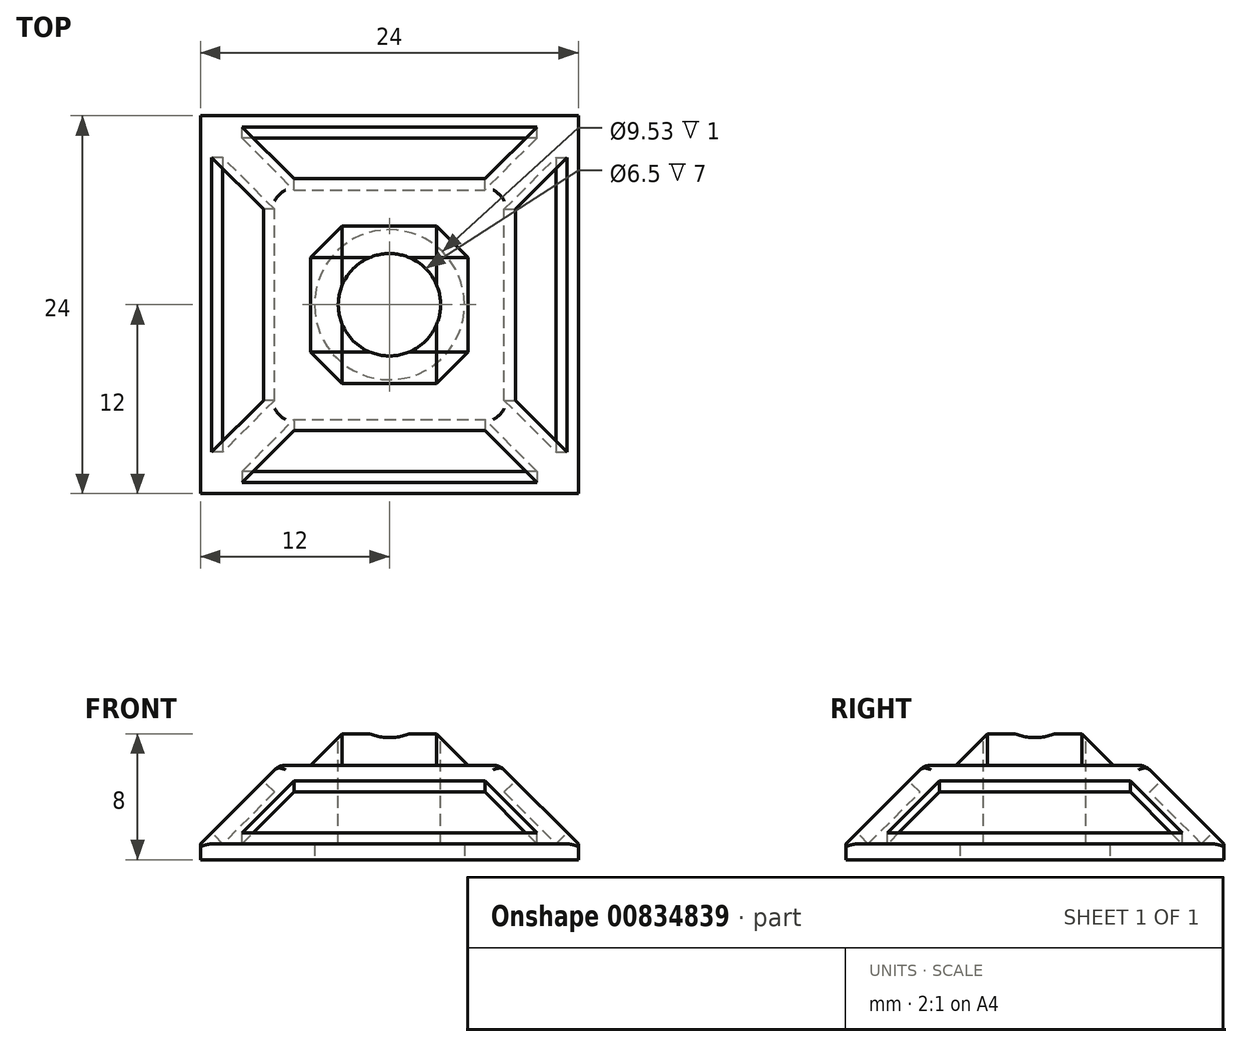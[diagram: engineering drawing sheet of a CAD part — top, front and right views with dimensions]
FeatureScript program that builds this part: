
annotation { "Feature Type Name" : "Feature", "Feature Type Description" : "" }
export const myFeature = defineFeature(function(context is Context, id is Id, definition is map)
    precondition{}
    {
        {
            var Q0;
            Q0=qCreatedBy(makeId("Top.planeOp"),FACE);
            var sketch = newSketch(context, id + "F0", { "sketchPlane" : qUnion([Q0])});
            skLineSegment(sketch, "E0.bottom", {"start": v(0, 0) * mm, "end": v(-12, 0) * mm});
            skLineSegment(sketch, "E0.top", {"start": v(0, 12) * mm, "end": v(-12, 12) * mm});
            skLineSegment(sketch, "E0.left", {"start": v(0, 0) * mm, "end": v(0, 12) * mm});
            skLineSegment(sketch, "E0.right", {"start": v(-12, 0) * mm, "end": v(-12, 12) * mm});
            skSolve(sketch);
        }
        {
            var Q0;
            Q0 = qSketchRegion(id + "F0", true);
            extrude(context, id + "F1", {"entities" : qUnion([Q0]), "depth" : 6 * mm, "offsetDistance" : 25 * mm});
        }
        {
            var Q0;
            Q0=makeQuery(id+"F1.opExtrude","CAP_FACE",FACE,{"disambiguationData":[OSD([sQuery(id+"F0.wireOp",EDGE,"E0.bottom"),sQuery(id+"F0.wireOp",EDGE,"E0.top"),sQuery(id+"F0.wireOp",EDGE,"E0.left"),sQuery(id+"F0.wireOp",EDGE,"E0.right")])],"isStart":true});
            var sketch = newSketch(context, id + "F2", { "sketchPlane" : qUnion([Q0])});
            skCircle(sketch, "E1", {"center": v(0, 0) * mm, "radius": 4.76 * mm});
            skSolve(sketch);
        }
        {
            var Q0;
            Q0 = qSketchRegion(id + "F2", true);
            extrude(context, id + "F3", {"entities" : qUnion([Q0]), "operationType" : NewBodyOperationType.REMOVE, "oppositeDirection" : true, "depth" : 1 * mm, "offsetDistance" : 25 * mm});
        }
        {
            var Q0;
            Q0=makeQuery(id+"F1.opExtrude","CAP_FACE",FACE,{"disambiguationData":[OSD([sQuery(id+"F0.wireOp",EDGE,"E0.bottom"),sQuery(id+"F0.wireOp",EDGE,"E0.top"),sQuery(id+"F0.wireOp",EDGE,"E0.left"),sQuery(id+"F0.wireOp",EDGE,"E0.right")])],"isStart":false});
            var sketch = newSketch(context, id + "F4", { "sketchPlane" : qUnion([Q0])});
            skLineSegment(sketch, "E2.bottom", {"start": v(0, 0) * mm, "end": v(-5, 0) * mm});
            skLineSegment(sketch, "E2.top", {"start": v(0, 5) * mm, "end": v(-5, 5) * mm});
            skLineSegment(sketch, "E2.left", {"start": v(0, 0) * mm, "end": v(0, 5) * mm});
            skLineSegment(sketch, "E2.right", {"start": v(-5, 0) * mm, "end": v(-5, 5) * mm});
            skSolve(sketch);
        }
        {
            var Q0;
            Q0 = qSketchRegion(id + "F4", true);
            extrude(context, id + "F5", {"entities" : qUnion([Q0]), "operationType" : NewBodyOperationType.ADD, "depth" : 2 * mm, "offsetDistance" : 25 * mm});
        }
        {
            var Q0;
            Q0=makeQuery(id+"F1.opExtrude","CAP_EDGE",EDGE,{"disambiguationData":[OSD([sQuery(id+"F0.wireOp",EDGE,"E0.right")])],"isStart":false});
            var Q1;
            Q1=makeQuery(id+"F1.opExtrude","CAP_EDGE",EDGE,{"disambiguationData":[OSD([sQuery(id+"F0.wireOp",EDGE,"E0.top")])],"isStart":false});
            chamfer(context, id + "F6", {"entities" : qUnion([Q0, Q1]), "width" : 5 * mm, "tangentPropagation" : true});
        }
        {
            var Q0;
            Q0=makeQuery(id+"F5.opExtrude","SWEPT_EDGE",EDGE,{"disambiguationData":[OSD([sQuery(id+"F4.wireOp",EDGE,"E2.top"),sQuery(id+"F4.wireOp",EDGE,"E2.right")])]});
            var Q1;
            Q1=makeQuery(id+"F16.opPattern","COPY",EDGE,{"derivedFrom":makeQuery(id+"F5.opExtrude","SWEPT_EDGE",EDGE,{"disambiguationData":[OSD([sQuery(id+"F4.wireOp",EDGE,"E2.top"),sQuery(id+"F4.wireOp",EDGE,"E2.right")])]}),"instanceName":"1"});
            var Q2;
            Q2=makeQuery(id+"F15.opPattern","COPY",EDGE,{"derivedFrom":makeQuery(id+"F5.opExtrude","SWEPT_EDGE",EDGE,{"disambiguationData":[OSD([sQuery(id+"F4.wireOp",EDGE,"E2.top"),sQuery(id+"F4.wireOp",EDGE,"E2.right")])]}),"instanceName":"1"});
            var Q3;
            Q3=makeQuery(id+"F16.opPattern","COPY",EDGE,{"derivedFrom":makeQuery(id+"F15.opPattern","COPY",EDGE,{"derivedFrom":makeQuery(id+"F5.opExtrude","SWEPT_EDGE",EDGE,{"disambiguationData":[OSD([sQuery(id+"F4.wireOp",EDGE,"E2.top"),sQuery(id+"F4.wireOp",EDGE,"E2.right")])]}),"instanceName":"1"}),"instanceName":"1"});
            var Q4;
            {var subQ0=makeQuery(id+"F5.opExtrude","CAP_EDGE",EDGE,{"disambiguationData":[OSD([sQuery(id+"F4.wireOp",EDGE,"E2.right")])],"isStart":false});Q4=makeQuery(id+"F15.boolean.opBoolean","MERGE",EDGE,{"derivedFrom":[subQ0,makeQuery(id+"F15.opPattern","COPY",EDGE,{"derivedFrom":subQ0,"instanceName":"1"})]});}
            var Q5;
            {var subQ0=makeQuery(id+"F5.opExtrude","CAP_EDGE",EDGE,{"disambiguationData":[OSD([sQuery(id+"F4.wireOp",EDGE,"E2.top")])],"isStart":false});Q5=makeQuery(id+"F16.boolean.opBoolean","MERGE",EDGE,{"derivedFrom":[subQ0,makeQuery(id+"F16.opPattern","COPY",EDGE,{"derivedFrom":subQ0,"instanceName":"1"})]});}
            var Q6;
            {var subQ0=makeQuery(id+"F5.opExtrude","CAP_EDGE",EDGE,{"disambiguationData":[OSD([sQuery(id+"F4.wireOp",EDGE,"E2.right")])],"isStart":false});Q6=makeQuery(id+"F16.opPattern","COPY",EDGE,{"derivedFrom":makeQuery(id+"F15.boolean.opBoolean","MERGE",EDGE,{"derivedFrom":[subQ0,makeQuery(id+"F15.opPattern","COPY",EDGE,{"derivedFrom":subQ0,"instanceName":"1"})]}),"instanceName":"1"});}
            var Q7;
            {var subQ0=makeQuery(id+"F15.opPattern","COPY",EDGE,{"derivedFrom":makeQuery(id+"F5.opExtrude","CAP_EDGE",EDGE,{"disambiguationData":[OSD([sQuery(id+"F4.wireOp",EDGE,"E2.top")])],"isStart":false}),"instanceName":"1"});Q7=makeQuery(id+"F16.boolean.opBoolean","MERGE",EDGE,{"derivedFrom":[subQ0,makeQuery(id+"F16.opPattern","COPY",EDGE,{"derivedFrom":subQ0,"instanceName":"1"})]});}
            chamfer(context, id + "F7", {"entities" : qUnion([Q0, Q1, Q2, Q3, Q4, Q5, Q6, Q7]), "width" : 2 * mm, "tangentPropagation" : true});
        }
        {
            var Q0;
            {var subQ0=sQuery(id+"F0.wireOp",EDGE,"E0.right");var subQ1=makeQuery(id+"F6.opChamfer","BLEND_EDGE",EDGE,{"blendedFrom":[makeQuery(id+"F1.opExtrude","CAP_EDGE",EDGE,{"disambiguationData":[OSD([subQ0])],"isStart":false}),makeQuery(id+"F1.opExtrude","CAP_FACE",FACE,{"disambiguationData":[OSD([sQuery(id+"F0.wireOp",EDGE,"E0.bottom"),sQuery(id+"F0.wireOp",EDGE,"E0.top"),sQuery(id+"F0.wireOp",EDGE,"E0.left"),subQ0])],"isStart":false})],"blendedInto":[makeQuery(id+"F1.opExtrude","CAP_FACE",FACE,{"disambiguationData":[OSD([sQuery(id+"F0.wireOp",EDGE,"E0.bottom"),sQuery(id+"F0.wireOp",EDGE,"E0.top"),sQuery(id+"F0.wireOp",EDGE,"E0.left"),subQ0])],"isStart":false})]});Q0=makeQuery(id+"F16.opPattern","COPY",EDGE,{"derivedFrom":makeQuery(id+"F15.boolean.opBoolean","MERGE",EDGE,{"derivedFrom":[subQ1,makeQuery(id+"F15.opPattern","COPY",EDGE,{"derivedFrom":subQ1,"instanceName":"1"})]}),"instanceName":"1"});}
            var Q1;
            {var subQ0=sQuery(id+"F0.wireOp",EDGE,"E0.top");var subQ1=makeQuery(id+"F6.opChamfer","BLEND_EDGE",EDGE,{"blendedFrom":[makeQuery(id+"F1.opExtrude","CAP_EDGE",EDGE,{"disambiguationData":[OSD([subQ0])],"isStart":false}),makeQuery(id+"F1.opExtrude","CAP_FACE",FACE,{"disambiguationData":[OSD([sQuery(id+"F0.wireOp",EDGE,"E0.bottom"),subQ0,sQuery(id+"F0.wireOp",EDGE,"E0.left"),sQuery(id+"F0.wireOp",EDGE,"E0.right")])],"isStart":false})],"blendedInto":[makeQuery(id+"F1.opExtrude","CAP_FACE",FACE,{"disambiguationData":[OSD([sQuery(id+"F0.wireOp",EDGE,"E0.bottom"),subQ0,sQuery(id+"F0.wireOp",EDGE,"E0.left"),sQuery(id+"F0.wireOp",EDGE,"E0.right")])],"isStart":false})]});Q1=makeQuery(id+"F16.boolean.opBoolean","MERGE",EDGE,{"derivedFrom":[subQ1,makeQuery(id+"F16.opPattern","COPY",EDGE,{"derivedFrom":subQ1,"instanceName":"1"})]});}
            var Q2;
            {var subQ0=sQuery(id+"F0.wireOp",EDGE,"E0.right");var subQ1=makeQuery(id+"F6.opChamfer","BLEND_EDGE",EDGE,{"blendedFrom":[makeQuery(id+"F1.opExtrude","CAP_EDGE",EDGE,{"disambiguationData":[OSD([subQ0])],"isStart":false}),makeQuery(id+"F1.opExtrude","CAP_FACE",FACE,{"disambiguationData":[OSD([sQuery(id+"F0.wireOp",EDGE,"E0.bottom"),sQuery(id+"F0.wireOp",EDGE,"E0.top"),sQuery(id+"F0.wireOp",EDGE,"E0.left"),subQ0])],"isStart":false})],"blendedInto":[makeQuery(id+"F1.opExtrude","CAP_FACE",FACE,{"disambiguationData":[OSD([sQuery(id+"F0.wireOp",EDGE,"E0.bottom"),sQuery(id+"F0.wireOp",EDGE,"E0.top"),sQuery(id+"F0.wireOp",EDGE,"E0.left"),subQ0])],"isStart":false})]});Q2=makeQuery(id+"F15.boolean.opBoolean","MERGE",EDGE,{"derivedFrom":[subQ1,makeQuery(id+"F15.opPattern","COPY",EDGE,{"derivedFrom":subQ1,"instanceName":"1"})]});}
            var Q3;
            {var subQ0=sQuery(id+"F0.wireOp",EDGE,"E0.top");var subQ1=makeQuery(id+"F15.opPattern","COPY",EDGE,{"derivedFrom":makeQuery(id+"F6.opChamfer","BLEND_EDGE",EDGE,{"blendedFrom":[makeQuery(id+"F1.opExtrude","CAP_EDGE",EDGE,{"disambiguationData":[OSD([subQ0])],"isStart":false}),makeQuery(id+"F1.opExtrude","CAP_FACE",FACE,{"disambiguationData":[OSD([sQuery(id+"F0.wireOp",EDGE,"E0.bottom"),subQ0,sQuery(id+"F0.wireOp",EDGE,"E0.left"),sQuery(id+"F0.wireOp",EDGE,"E0.right")])],"isStart":false})],"blendedInto":[makeQuery(id+"F1.opExtrude","CAP_FACE",FACE,{"disambiguationData":[OSD([sQuery(id+"F0.wireOp",EDGE,"E0.bottom"),subQ0,sQuery(id+"F0.wireOp",EDGE,"E0.left"),sQuery(id+"F0.wireOp",EDGE,"E0.right")])],"isStart":false})]}),"instanceName":"1"});Q3=makeQuery(id+"F16.boolean.opBoolean","MERGE",EDGE,{"derivedFrom":[subQ1,makeQuery(id+"F16.opPattern","COPY",EDGE,{"derivedFrom":subQ1,"instanceName":"1"})]});}
            var Q4;
            Q4=makeQuery(id+"F6.opChamfer","BLEND_EDGE",EDGE,{"blendedFrom":[makeQuery(id+"F1.opExtrude","CAP_EDGE",EDGE,{"disambiguationData":[OSD([sQuery(id+"F0.wireOp",EDGE,"E0.top")])],"isStart":false}),makeQuery(id+"F1.opExtrude","CAP_EDGE",EDGE,{"disambiguationData":[OSD([sQuery(id+"F0.wireOp",EDGE,"E0.right")])],"isStart":false})],"blendedInto":[]});
            var Q5;
            Q5=makeQuery(id+"F16.opPattern","COPY",EDGE,{"derivedFrom":makeQuery(id+"F6.opChamfer","BLEND_EDGE",EDGE,{"blendedFrom":[makeQuery(id+"F1.opExtrude","CAP_EDGE",EDGE,{"disambiguationData":[OSD([sQuery(id+"F0.wireOp",EDGE,"E0.top")])],"isStart":false}),makeQuery(id+"F1.opExtrude","CAP_EDGE",EDGE,{"disambiguationData":[OSD([sQuery(id+"F0.wireOp",EDGE,"E0.right")])],"isStart":false})],"blendedInto":[]}),"instanceName":"1"});
            var Q6;
            Q6=makeQuery(id+"F16.opPattern","COPY",EDGE,{"derivedFrom":makeQuery(id+"F15.opPattern","COPY",EDGE,{"derivedFrom":makeQuery(id+"F6.opChamfer","BLEND_EDGE",EDGE,{"blendedFrom":[makeQuery(id+"F1.opExtrude","CAP_EDGE",EDGE,{"disambiguationData":[OSD([sQuery(id+"F0.wireOp",EDGE,"E0.top")])],"isStart":false}),makeQuery(id+"F1.opExtrude","CAP_EDGE",EDGE,{"disambiguationData":[OSD([sQuery(id+"F0.wireOp",EDGE,"E0.right")])],"isStart":false})],"blendedInto":[]}),"instanceName":"1"}),"instanceName":"1"});
            var Q7;
            Q7=makeQuery(id+"F15.opPattern","COPY",EDGE,{"derivedFrom":makeQuery(id+"F6.opChamfer","BLEND_EDGE",EDGE,{"blendedFrom":[makeQuery(id+"F1.opExtrude","CAP_EDGE",EDGE,{"disambiguationData":[OSD([sQuery(id+"F0.wireOp",EDGE,"E0.top")])],"isStart":false}),makeQuery(id+"F1.opExtrude","CAP_EDGE",EDGE,{"disambiguationData":[OSD([sQuery(id+"F0.wireOp",EDGE,"E0.right")])],"isStart":false})],"blendedInto":[]}),"instanceName":"1"});
            fillet(context, id + "F8", {"entities" : qUnion([Q0, Q1, Q2, Q3, Q4, Q5, Q6, Q7]), "tangentPropagation" : true, "radius" : 1 * mm, "defaultsChanged" : true, "vertexSettings" : [], "allowEdgeOverflow" : false});
        }
        {
            var Q0;
            Q0=makeQuery(id+"F6.opChamfer","BLEND_FACE",FACE,{"disambiguationData":[OSD([sQuery(id+"F0.wireOp",EDGE,"E0.top")])]});
            var sketch = newSketch(context, id + "F9", { "sketchPlane" : qUnion([Q0])});
            skLineSegment(sketch, "E3.0", {"start": v(9.36, -6.78) * mm, "end": v(6.07, -2.12) * mm});
            skLineSegment(sketch, "E3.1", {"start": v(0, -6.78) * mm, "end": v(9.36, -6.78) * mm});
            skLineSegment(sketch, "E3.2", {"start": v(0, -2.12) * mm, "end": v(0, -6.78) * mm});
            skLineSegment(sketch, "E3.3", {"start": v(6.07, -2.12) * mm, "end": v(0, -2.12) * mm});
            skSolve(sketch);
        }
        {
            var Q0;
            Q0 = qSketchRegion(id + "F9", true);
            extrude(context, id + "F10", {"entities" : qUnion([Q0]), "operationType" : NewBodyOperationType.REMOVE, "oppositeDirection" : true, "depth" : 1 * mm, "offsetDistance" : 25 * mm});
        }
        {
            var Q0;
            Q0=makeQuery(id+"F6.opChamfer","BLEND_FACE",FACE,{"disambiguationData":[OSD([sQuery(id+"F0.wireOp",EDGE,"E0.right")])]});
            var sketch = newSketch(context, id + "F11", { "sketchPlane" : qUnion([Q0])});
            skLineSegment(sketch, "E4.0", {"start": v(0, -2.12) * mm, "end": v(0, -6.78) * mm});
            skLineSegment(sketch, "E4.1", {"start": v(0, -2.12) * mm, "end": v(-6.07, -2.12) * mm});
            skLineSegment(sketch, "E4.2", {"start": v(-6.07, -2.12) * mm, "end": v(-9.36, -6.78) * mm});
            skLineSegment(sketch, "E4.3", {"start": v(-9.36, -6.78) * mm, "end": v(0, -6.78) * mm});
            skSolve(sketch);
        }
        {
            var Q0;
            Q0 = qSketchRegion(id + "F11", true);
            extrude(context, id + "F12", {"entities" : qUnion([Q0]), "operationType" : NewBodyOperationType.REMOVE, "oppositeDirection" : true, "depth" : 1 * mm, "offsetDistance" : 25 * mm});
        }
        {
            var Q0;
            Q0=makeQuery(id+"F5.opExtrude","CAP_FACE",FACE,{"disambiguationData":[OSD([sQuery(id+"F4.wireOp",EDGE,"E2.bottom"),sQuery(id+"F4.wireOp",EDGE,"E2.top"),sQuery(id+"F4.wireOp",EDGE,"E2.left"),sQuery(id+"F4.wireOp",EDGE,"E2.right")])],"isStart":false});
            var sketch = newSketch(context, id + "F13", { "sketchPlane" : qUnion([Q0])});
            skCircle(sketch, "E5", {"center": v(0, 0) * mm, "radius": 3.25 * mm});
            skSolve(sketch);
        }
        {
            var Q0;
            Q0 = qSketchRegion(id + "F13", true);
            var Q1;
            Q1=makeQuery(id+"F3.boolean.opBoolean","COPY",FACE,{"derivedFrom":makeQuery(id+"F3.opExtrude","CAP_FACE",FACE,{"disambiguationData":[OSD([sQuery(id+"F2.wireOp",EDGE,"E1")])],"isStart":false})});
            extrude(context, id + "F14", {"entities" : qUnion([Q0]), "operationType" : NewBodyOperationType.REMOVE, "endBound" : BoundingType.UP_TO_SURFACE, "oppositeDirection" : true, "depth" : 25 * mm, "endBoundEntityFace" : qUnion([Q1]), "offsetDistance" : 25 * mm});
        }
        {
            var Q0;
            Q0=makeQuery(id+"F1.opExtrude","SWEPT_BODY",BODY,{"disambiguationData":[OSD([sQuery(id+"F0.wireOp",EDGE,"E0.bottom"),sQuery(id+"F0.wireOp",EDGE,"E0.top"),sQuery(id+"F0.wireOp",EDGE,"E0.left"),sQuery(id+"F0.wireOp",EDGE,"E0.right")])]});
            var Q1;
            Q1=qCreatedBy(makeId("Front.planeOp"),FACE);
            mirror(context, id + "F15", {"operationType" : NewBodyOperationType.ADD, "entities" : qUnion([Q0]), "mirrorPlane" : qUnion([Q1])});
        }
        {
            var Q0;
            Q0=makeQuery(id+"F1.opExtrude","SWEPT_BODY",BODY,{"disambiguationData":[OSD([sQuery(id+"F0.wireOp",EDGE,"E0.bottom"),sQuery(id+"F0.wireOp",EDGE,"E0.top"),sQuery(id+"F0.wireOp",EDGE,"E0.left"),sQuery(id+"F0.wireOp",EDGE,"E0.right")])]});
            var Q1;
            Q1=qCreatedBy(makeId("Right.planeOp"),FACE);
            mirror(context, id + "F16", {"operationType" : NewBodyOperationType.ADD, "entities" : qUnion([Q0]), "mirrorPlane" : qUnion([Q1])});
        }
    });
